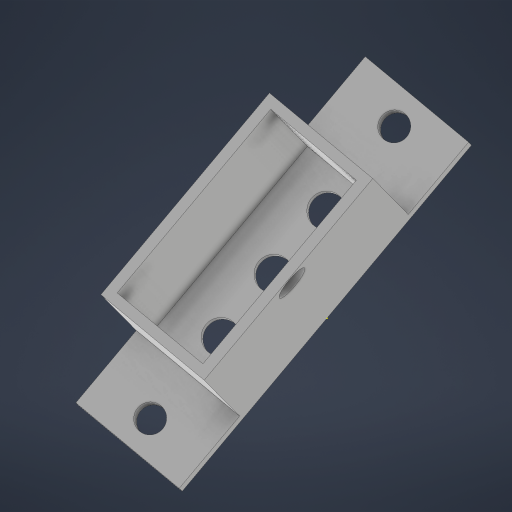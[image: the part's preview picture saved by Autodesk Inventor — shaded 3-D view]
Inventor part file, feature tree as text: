
AUTODESK INVENTOR PART (.ipt)
format: ipt  version: 2023 (Build 270158000, 158)  size: 232,960 bytes
history: native  units: mm
features: sketch x5, extrude x4, shell x1
ambient origin geometry x8: Origin, YZ Plane, XZ Plane, XY Plane, X Axis, Y Axis, Z Axis, Center Point
bodies: Solid1 (feature_tree)
feature tree (10):
  extrude  "Extrusion1"  Depth=35.0mm
  extrude  "Extrusion2"  Depth=67.0mm
  shell  "Shell1"  Thickness=60.0mm
  extrude  "Extrusion3"  Depth=10.0mm
  sketch  "Sketch4"  dims[d15=10.0mm d16=10.0mm]
  extrude  "Extrusion4"  Depth=10.0mm
  sketch  "Sketch1"  dims[d0=115.0mm d1=35.0mm]
  sketch  "Sketch2"  dims[d8=5.0mm d9=0.0mm d10=67.0mm d11=60.0mm d12=0.0mm]
  sketch  "Sketch3"  dims[d13=3.0mm d14=10.0mm]
  sketch  "Sketch5"  dims[d17=21.0mm d18=21.0mm d19=8.5mm d20=8.5mm d21=97.0mm d22=9.0mm d23=9.0mm d24=0.0mm d25=0.0mm d26=10.0mm d27=6.0mm d28=3.0mm d29=0.0mm d30=0.25mm d31=0.375mm d32=14.3117mm d33=0.75mm d34=20.594885mm d35=0.0625mm d36=0.75mm d37=0.375mm]
